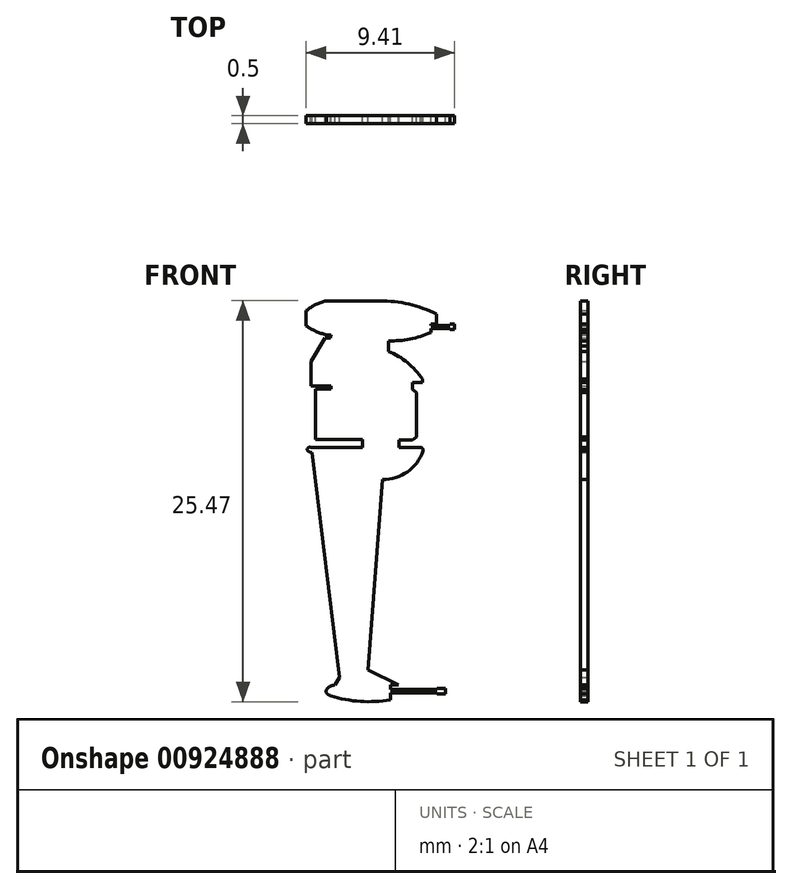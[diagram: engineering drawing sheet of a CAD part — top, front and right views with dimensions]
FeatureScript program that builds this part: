
annotation { "Feature Type Name" : "Feature", "Feature Type Description" : "" }
export const myFeature = defineFeature(function(context is Context, id is Id, definition is map)
    precondition{}
    {
        {
            var Q0;
            Q0=qCreatedBy(makeId("Front.planeOp"),FACE);
            var sketch = newSketch(context, id + "F0", { "sketchPlane" : qUnion([Q0])});
            skLineSegment(sketch, "E0", {"start": v(-43.8, 8.74) * mm, "end": v(-42.04, -5.53) * mm});
            skLineSegment(sketch, "E1", {"start": v(-42.04, -5.53) * mm, "end": v(-42.35, -6.03) * mm});
            skLineSegment(sketch, "E2", {"start": v(-38.82, -6.03) * mm, "end": v(-38.3, -6.03) * mm});
            skLineSegment(sketch, "E3", {"start": v(-38.3, -6.03) * mm, "end": v(-40.23, -5.08) * mm});
            skLineSegment(sketch, "E4", {"start": v(-40.23, -5.08) * mm, "end": v(-39.3, 7.03) * mm});
            skArc(sketch, "E5", {"start": v(-39.3, 7.03) * mm, "mid": v(-37.73, 7.52) * mm, "end": v(-36.74, 8.83) * mm});
            skPoint(sketch, "E5.third.point", {"position": v(-41.96, 9.8) * mm});
            skLineSegment(sketch, "E6", {"start": v(-37.43, 13.2) * mm, "end": v(-36.79, 13.2) * mm});
            skLineSegment(sketch, "E7", {"start": v(-36.79, 13.2) * mm, "end": v(-36.79, 13.4) * mm});
            skArc(sketch, "E8", {"start": v(-36.79, 13.4) * mm, "mid": v(-37.73, 14.45) * mm, "end": v(-38.94, 15.17) * mm});
            skPoint(sketch, "E8.third.point", {"position": v(-44.82, 12.98) * mm});
            skLineSegment(sketch, "E9", {"start": v(-38.94, 15.17) * mm, "end": v(-38.94, 15.84) * mm});
            skLineSegment(sketch, "E10", {"start": v(-36.25, 16.36) * mm, "end": v(-36.25, 16.9) * mm});
            skLineSegment(sketch, "E11", {"start": v(-36.25, 16.9) * mm, "end": v(-35.87, 16.9) * mm});
            skLineSegment(sketch, "E12", {"start": v(-35.87, 16.9) * mm, "end": v(-35.87, 17.54) * mm});
            skArc(sketch, "E13", {"start": v(-38.94, 15.84) * mm, "mid": v(-37.57, 15.94) * mm, "end": v(-36.25, 16.36) * mm});
            skPoint(sketch, "E13.third.point", {"position": v(-43.92, 18.83) * mm});
            skLineSegment(sketch, "E14", {"start": v(-39.49, 18.38) * mm, "end": v(-41.8, 18.38) * mm});
            skLineSegment(sketch, "E15", {"start": v(-41.8, 18.38) * mm, "end": v(-42.88, 18.38) * mm});
            skLineSegment(sketch, "E16", {"start": v(-42.88, 16.22) * mm, "end": v(-42.58, 16.22) * mm});
            skLineSegment(sketch, "E17", {"start": v(-42.58, 16.22) * mm, "end": v(-42.61, 16) * mm});
            skLineSegment(sketch, "E18", {"start": v(-42.61, 16) * mm, "end": v(-42.96, 16) * mm});
            skLineSegment(sketch, "E19", {"start": v(-42.96, 16) * mm, "end": v(-43.85, 14.52) * mm});
            skLineSegment(sketch, "E20", {"start": v(-43.85, 14.52) * mm, "end": v(-43.85, 12.96) * mm});
            skLineSegment(sketch, "E21", {"start": v(-43.85, 12.96) * mm, "end": v(-42.6, 12.96) * mm});
            skLineSegment(sketch, "E22", {"start": v(-42.6, 12.96) * mm, "end": v(-42.6, 12.76) * mm});
            skLineSegment(sketch, "E23", {"start": v(-42.6, 12.76) * mm, "end": v(-43.58, 12.76) * mm});
            skLineSegment(sketch, "E24", {"start": v(-43.58, 12.76) * mm, "end": v(-43.58, 9.58) * mm});
            skLineSegment(sketch, "E25", {"start": v(-38.26, 9.08) * mm, "end": v(-38.26, 9.55) * mm});
            skLineSegment(sketch, "E26", {"start": v(-38.26, 9.55) * mm, "end": v(-37.43, 9.55) * mm});
            skLineSegment(sketch, "E27", {"start": v(-37.43, 9.55) * mm, "end": v(-37.15, 9.72) * mm});
            skLineSegment(sketch, "E28", {"start": v(-37.15, 9.72) * mm, "end": v(-37.15, 12.55) * mm});
            skLineSegment(sketch, "E29", {"start": v(-37.15, 12.55) * mm, "end": v(-37.43, 12.74) * mm});
            skLineSegment(sketch, "E30", {"start": v(-37.43, 12.74) * mm, "end": v(-37.43, 13.2) * mm});
            skArc(sketch, "E31", {"start": v(-44.17, 16.8) * mm, "mid": v(-43.55, 16.44) * mm, "end": v(-42.88, 16.22) * mm});
            skPoint(sketch, "E31.second.point", {"position": v(-44.17, 16.8) * mm});
            skPoint(sketch, "E31.third.point", {"position": v(-40.1, 16.86) * mm});
            skLineSegment(sketch, "E32", {"start": v(-44.17, 16.8) * mm, "end": v(-44.17, 17.75) * mm});
            skArc(sketch, "E33", {"start": v(-38.93, 15.17) * mm, "mid": v(-38.93, 15.34) * mm, "end": v(-38.94, 15.5) * mm});
            skPoint(sketch, "E33.third.point", {"position": v(-38.94, 15.5) * mm});
            skArc(sketch, "E34.trimOffspring", {"start": v(-42.88, 18.38) * mm, "mid": v(-43.56, 18.13) * mm, "end": v(-44.17, 17.75) * mm});
            skArc(sketch, "E35", {"start": v(-35.87, 17.54) * mm, "mid": v(-37.63, 18.16) * mm, "end": v(-39.49, 18.38) * mm});
            skArc(sketch, "E36", {"start": v(-42.35, -6.03) * mm, "mid": v(-42.68, -6.13) * mm, "end": v(-42.9, -6.4) * mm});
            skLineSegment(sketch, "E37", {"start": v(-42.9, -6.4) * mm, "end": v(-42.9, -6.48) * mm});
            skArc(sketch, "E38", {"start": v(-42.9, -6.48) * mm, "mid": v(-42.78, -6.63) * mm, "end": v(-42.6, -6.7) * mm});
            skArc(sketch, "E39", {"start": v(-42.6, -6.7) * mm, "mid": v(-40.73, -7.07) * mm, "end": v(-38.82, -6.97) * mm});
            skLineSegment(sketch, "E40", {"start": v(-38.82, -6.97) * mm, "end": v(-38.82, -6.03) * mm});
            skLineSegment(sketch, "E41", {"start": v(-38.82, -6.31) * mm, "end": v(-35.85, -6.31) * mm});
            skLineSegment(sketch, "E42", {"start": v(-35.85, -6.31) * mm, "end": v(-35.85, -6.53) * mm});
            skLineSegment(sketch, "E43", {"start": v(-35.85, -6.53) * mm, "end": v(-38.82, -6.53) * mm});
            skLineSegment(sketch, "E44", {"start": v(-35.85, -6.53) * mm, "end": v(-35.85, -6.6) * mm});
            skLineSegment(sketch, "E45", {"start": v(-35.85, -6.6) * mm, "end": v(-35.32, -6.6) * mm});
            skLineSegment(sketch, "E46", {"start": v(-35.32, -6.6) * mm, "end": v(-35.32, -6.24) * mm});
            skLineSegment(sketch, "E47", {"start": v(-35.85, -6.31) * mm, "end": v(-35.85, -6.24) * mm});
            skLineSegment(sketch, "E48", {"start": v(-35.32, -6.24) * mm, "end": v(-35.85, -6.24) * mm});
            skLineSegment(sketch, "E49.trimOffspring", {"start": v(-43.26, 9.08) * mm, "end": v(-43.9, 9.08) * mm});
            skLineSegment(sketch, "E50", {"start": v(-36.25, 16.8) * mm, "end": v(-35.04, 16.8) * mm});
            skLineSegment(sketch, "E51", {"start": v(-35.04, 16.8) * mm, "end": v(-35.04, 16.6) * mm});
            skLineSegment(sketch, "E52", {"start": v(-35.04, 16.6) * mm, "end": v(-36.25, 16.6) * mm});
            skLineSegment(sketch, "E53", {"start": v(-35.04, 16.8) * mm, "end": v(-35.04, 16.89) * mm});
            skLineSegment(sketch, "E54", {"start": v(-35.04, 16.89) * mm, "end": v(-34.76, 16.89) * mm});
            skLineSegment(sketch, "E55", {"start": v(-34.76, 16.89) * mm, "end": v(-34.76, 16.54) * mm});
            skLineSegment(sketch, "E56", {"start": v(-34.76, 16.54) * mm, "end": v(-35.04, 16.54) * mm});
            skLineSegment(sketch, "E57", {"start": v(-35.04, 16.54) * mm, "end": v(-35.04, 16.6) * mm});
            skPoint(sketch, "E58.orphan", {"position": v(-41.8, 16.22) * mm});
            skArc(sketch, "E59", {"start": v(-36.74, 8.83) * mm, "mid": v(-36.77, 9) * mm, "end": v(-36.92, 9.08) * mm});
            skLineSegment(sketch, "E60", {"start": v(-36.92, 9.08) * mm, "end": v(-38.26, 9.08) * mm});
            skArc(sketch, "E61", {"start": v(-43.9, 9.08) * mm, "mid": v(-44.03, 9.05) * mm, "end": v(-44.1, 8.94) * mm});
            skArc(sketch, "E62", {"start": v(-44.1, 8.94) * mm, "mid": v(-43.98, 8.79) * mm, "end": v(-43.8, 8.74) * mm});
            skLineSegment(sketch, "E63.top", {"start": v(-43.26, 9.08) * mm, "end": v(-40.58, 9.08) * mm});
            skLineSegment(sketch, "E63.right", {"start": v(-40.58, 9.58) * mm, "end": v(-40.58, 9.08) * mm});
            skPoint(sketch, "E63.bottom.start.orphan", {"position": v(-43.26, 9.58) * mm});
            skLineSegment(sketch, "E64", {"start": v(-40.58, 9.58) * mm, "end": v(-43.58, 9.58) * mm});
            skLineSegment(sketch, "E65", {"start": v(-46.23, 21.09) * mm, "end": v(-46.23, -8.65) * mm});
            skSolve(sketch);
        }
        {
            var Q0;
            Q0 = qSketchRegion(id + "F0", true);
            extrude(context, id + "F1", {"entities" : qUnion([Q0]), "depth" : .5 * mm, "offsetDistance" : 25 * mm});
        }
    });
